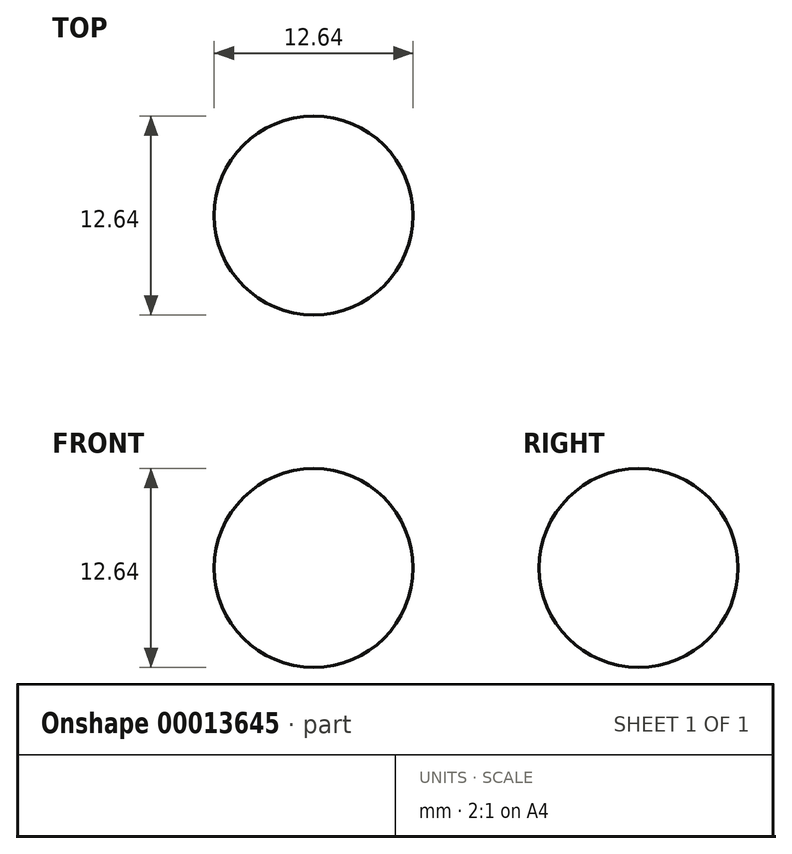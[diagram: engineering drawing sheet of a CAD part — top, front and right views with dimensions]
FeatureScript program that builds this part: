
annotation { "Feature Type Name" : "Feature", "Feature Type Description" : "" }
export const myFeature = defineFeature(function(context is Context, id is Id, definition is map)
    precondition{}
    {
        {
            var Q0;
            Q0=qCreatedBy(makeId("Top.planeOp"),FACE);
            var sketch = newSketch(context, id + "F0", { "sketchPlane" : qUnion([Q0])});
            skCircle(sketch, "E0", {"center": v(0, 0) * mm, "radius": 6.35 * mm});
            skCircle(sketch, "E1", {"center": v(0, 0) * mm, "radius": 6.32 * mm});
            skLineSegment(sketch, "E2", {"start": v(0, 6.35) * mm, "end": v(0, -6.35) * mm});
            skSolve(sketch);
        }
        {
            var Q0;
            {var subQ0=sQuery(id+"F0.wireOp",EDGE,"E2");var subQ1=sQuery(id+"F0.wireOp",EDGE,"E1");var subQ3=makeQuery(id+"F0.imprint","INTERSECT",VERTEX,{"disambiguationData":[OD(0.0)],"derivedFrom":[subQ1,subQ0]});Q0=makeQuery(id+"F0.imprint","IMPRINT",FACE,{"disambiguationData":[TD([[makeQuery(id+"F0.imprint","IMPRINT",EDGE,{"disambiguationData":[TD([[subQ3,1.0]])],"derivedFrom":subQ1}),1.0]])]});}
            var Q1;
            Q1=sQuery(id+"F0.wireOp",EDGE,"E2");
            revolve(context, id + "F1", {"entities" : qUnion([Q0]), "axis" : qUnion([Q1]), "revolveType" : RevolveType.FULL});
        }
    });
